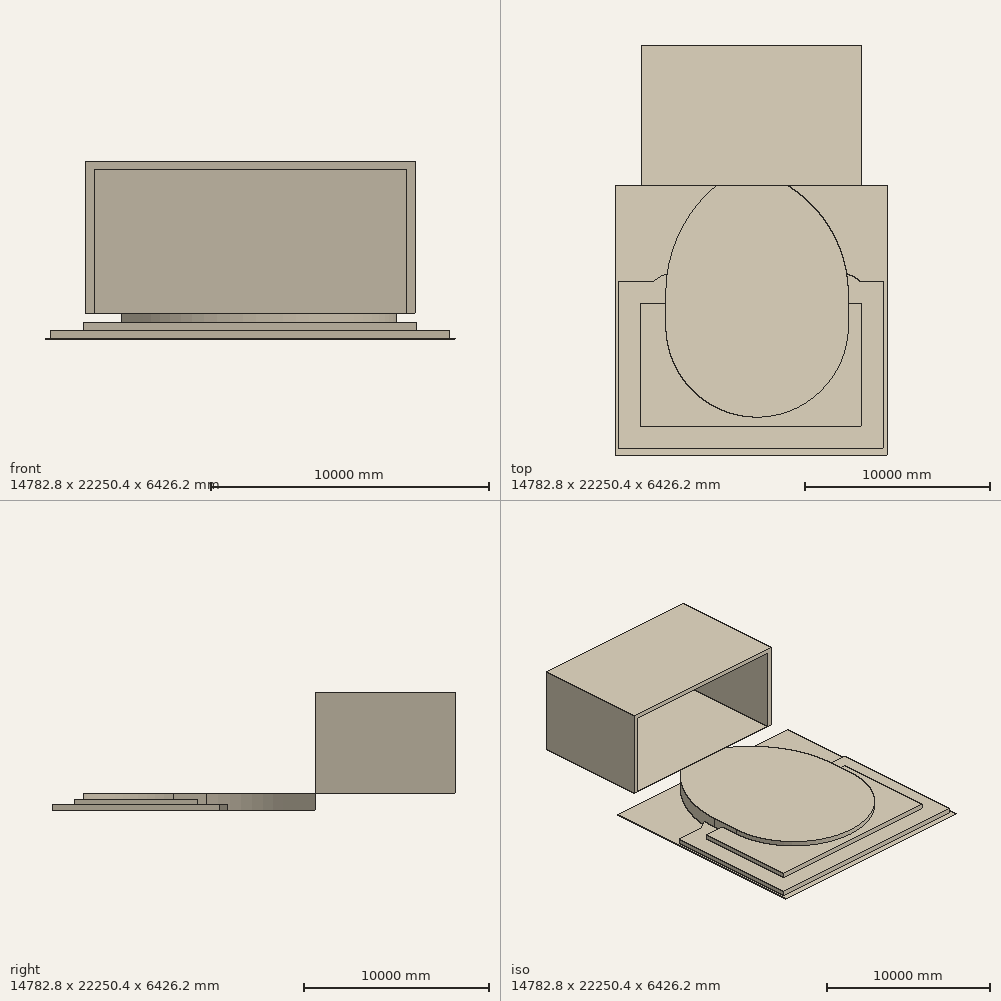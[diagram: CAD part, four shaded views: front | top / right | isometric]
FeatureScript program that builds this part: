
annotation { "Feature Type Name" : "Feature", "Feature Type Description" : "" }
export const myFeature = defineFeature(function(context is Context, id is Id, definition is map)
    precondition{}
    {
        {
            var Q0;
            Q0=qCreatedBy(makeId("Top.planeOp"),FACE);
            var sketch = newSketch(context, id + "F0", { "sketchPlane" : qUnion([Q0])});
            skLineSegment(sketch, "E0.bottom", {"start": v(-5413.18, 0) * mm, "end": v(9369.62, 0) * mm});
            skLineSegment(sketch, "E0.top", {"start": v(-5413.18, -14630.4) * mm, "end": v(9369.62, -14630.4) * mm});
            skLineSegment(sketch, "E0.left", {"start": v(-5413.18, 0) * mm, "end": v(-5413.18, -14630.4) * mm});
            skLineSegment(sketch, "E0.right", {"start": v(9369.62, 0) * mm, "end": v(9369.62, -14630.4) * mm});
            skSolve(sketch);
        }
        {
            var Q0;
            Q0=makeQuery(id+"F0.imprint","IMPRINT",FACE,{"disambiguationData":[TD([[makeQuery(id+"F0.imprint","IMPRINT",EDGE,{"derivedFrom":sQuery(id+"F0.wireOp",EDGE,"E0.bottom")}),-1.0]])]});
            extrude(context, id + "F1", {"entities" : qUnion([Q0]), "oppositeDirection" : true, "depth" : 25.4 * mm});
        }
        {
            var Q0;
            Q0=makeQuery(id+"F1.opExtrude","CAP_FACE",FACE,{"disambiguationData":[OSD([sQuery(id+"F0.wireOp",EDGE,"E0.bottom"),sQuery(id+"F0.wireOp",EDGE,"E0.top"),sQuery(id+"F0.wireOp",EDGE,"E0.left"),sQuery(id+"F0.wireOp",EDGE,"E0.right")])],"isStart":true});
            var sketch = newSketch(context, id + "F2", { "sketchPlane" : qUnion([Q0])});
            skArc(sketch, "E1", {"start": v(73.22, 0) * mm, "mid": v(-1968.15, -2645.58) * mm, "end": v(-2669.49, -5912.75) * mm});
            skArc(sketch, "E2.MirrorCS", {"start": v(3984.82, 0) * mm, "mid": v(6363.8, -2518.13) * mm, "end": v(7235.98, -5870.7) * mm});
            skLineSegment(sketch, "E3", {"start": v(2028.45, -12547.65) * mm, "end": v(2526.63, -12484.75) * mm});
            skArc(sketch, "E4", {"start": v(-2673.59, -7535.85) * mm, "mid": v(2315.04, -12554.16) * mm, "end": v(7241.23, -7474.54) * mm});
            skLineSegment(sketch, "E5", {"start": v(-2673.59, -7535.85) * mm, "end": v(-2668.95, -5701.93) * mm});
            skLineSegment(sketch, "E6", {"start": v(7241.92, -7684.86) * mm, "end": v(7235.98, -5870.7) * mm});
            skSolve(sketch);
        }
        {
            var Q0;
            {var subQ1=sQuery(id+"F2.wireOp",EDGE,"E2.MirrorCS");Q0=makeQuery(id+"F2.imprint","IMPRINT",FACE,{"disambiguationData":[TD([[makeQuery(id+"F2.imprint","IMPRINT",EDGE,{"derivedFrom":subQ1}),1.0]])]});}
            extrude(context, id + "F3", {"entities" : qUnion([Q0]), "operationType" : NewBodyOperationType.ADD, "depth" : 914.4 * mm});
        }
        {
            var Q0;
            Q0=makeQuery(id+"F0.imprint","IMPRINT",FACE,{"disambiguationData":[TD([[makeQuery(id+"F0.imprint","IMPRINT",EDGE,{"derivedFrom":sQuery(id+"F0.wireOp",EDGE,"E0.bottom")}),-1.0]])]});
            var sketch = newSketch(context, id + "F4", { "sketchPlane" : qUnion([Q0])});
            skLineSegment(sketch, "E7.2", {"start": v(-1479.8, -7544.99) * mm, "end": v(-1476.86, -6378.62) * mm});
            skArc(sketch, "E7.3", {"start": v(6047.48, -7491.98) * mm, "mid": v(2310.9, -11360.37) * mm, "end": v(-1479.8, -7544.99) * mm});
            skLineSegment(sketch, "E7.8", {"start": v(6043.84, -6378.63) * mm, "end": v(6047.48, -7491.98) * mm});
            skArc(sketch, "E8", {"start": v(-1476.86, -6378.62) * mm, "mid": v(-2073.76, -5892.8) * mm, "end": v(-2670.66, -6378.62) * mm});
            skArc(sketch, "E9", {"start": v(7237.65, -6378.63) * mm, "mid": v(6640.74, -5892.8) * mm, "end": v(6043.84, -6378.63) * mm});
            skLineSegment(sketch, "E10", {"start": v(-2670.66, -6378.62) * mm, "end": v(-4050.4, -6378.62) * mm});
            skLineSegment(sketch, "E11", {"start": v(-4050.4, -6378.62) * mm, "end": v(-4050.4, -13055.66) * mm});
            skLineSegment(sketch, "E12", {"start": v(-4050.4, -13055.66) * mm, "end": v(7961.94, -13055.66) * mm});
            skLineSegment(sketch, "E13", {"start": v(7961.94, -13055.66) * mm, "end": v(7961.94, -6378.62) * mm});
            skLineSegment(sketch, "E14", {"start": v(7961.94, -6378.62) * mm, "end": v(7237.65, -6378.63) * mm});
            skSolve(sketch);
        }
        {
            var Q0;
            Q0 = qSketchRegion(id + "F4", true);
            var Q1;
            Q1=sQuery(id+"F4.wireOp",EDGE,"E11");
            var Q2;
            Q2=sQuery(id+"F4.wireOp",EDGE,"E14");
            var Q3;
            Q3=sQuery(id+"F4.wireOp",EDGE,"E7.3");
            var Q4;
            Q4=sQuery(id+"F4.wireOp",EDGE,"E7.2");
            var Q5;
            Q5=sQuery(id+"F4.wireOp",EDGE,"E10");
            var Q6;
            Q6=sQuery(id+"F4.wireOp",EDGE,"E13");
            var Q7;
            Q7=sQuery(id+"F4.wireOp",EDGE,"E8");
            var Q8;
            Q8=sQuery(id+"F4.wireOp",EDGE,"E12");
            var Q9;
            Q9=sQuery(id+"F4.wireOp",EDGE,"E7.8");
            var Q10;
            Q10=sQuery(id+"F4.wireOp",EDGE,"E9");
            extrude(context, id + "F5", {"entities" : qUnion([Q0]), "surfaceEntities" : qUnion([Q1, Q2, Q3, Q4, Q5, Q6, Q7, Q8, Q9, Q10]), "depth" : 609.6 * mm});
        }
        {
            var Q0;
            Q0=makeQuery(id+"F0.imprint","IMPRINT",FACE,{"disambiguationData":[TD([[makeQuery(id+"F0.imprint","IMPRINT",EDGE,{"derivedFrom":sQuery(id+"F0.wireOp",EDGE,"E0.bottom")}),-1.0]])]});
            var sketch = newSketch(context, id + "F6", { "sketchPlane" : qUnion([Q0])});
            skLineSegment(sketch, "E15.0", {"start": v(-5244.2, -14249.46) * mm, "end": v(9155.74, -14249.46) * mm});
            skLineSegment(sketch, "E15.1", {"start": v(-5244.2, -5184.82) * mm, "end": v(-5244.2, -14249.46) * mm});
            skLineSegment(sketch, "E15.2", {"start": v(9155.74, -14249.46) * mm, "end": v(9155.74, -5184.81) * mm});
            skLineSegment(sketch, "E15.3", {"start": v(-3305.12, -5184.82) * mm, "end": v(-5244.2, -5184.82) * mm});
            skArc(sketch, "E15.4", {"start": v(-282.83, -6290.67) * mm, "mid": v(-1454.08, -4808.8) * mm, "end": v(-3305.12, -5184.82) * mm});
            skLineSegment(sketch, "E15.5", {"start": v(-286.03, -7555.2) * mm, "end": v(-282.83, -6290.67) * mm});
            skLineSegment(sketch, "E15.6", {"start": v(9155.74, -5184.81) * mm, "end": v(7872.1, -5184.83) * mm});
            skArc(sketch, "E15.7", {"start": v(7872.1, -5184.83) * mm, "mid": v(6020.8, -4808.9) * mm, "end": v(4849.75, -6291.24) * mm});
            skLineSegment(sketch, "E15.8", {"start": v(4849.75, -6291.24) * mm, "end": v(4853.74, -7511.8) * mm});
            skArc(sketch, "E15.9", {"start": v(4853.74, -7511.8) * mm, "mid": v(2306.09, -10166.57) * mm, "end": v(-286.03, -7555.2) * mm});
            skSolve(sketch);
        }
        {
            var Q0;
            Q0 = qSketchRegion(id + "F6", true);
            extrude(context, id + "F7", {"entities" : qUnion([Q0]), "depth" : 304.8 * mm});
        }
        {
            var Q0;
            Q0=makeQuery(id+"F0.imprint","IMPRINT",FACE,{"disambiguationData":[TD([[makeQuery(id+"F0.imprint","IMPRINT",EDGE,{"derivedFrom":sQuery(id+"F0.wireOp",EDGE,"E0.bottom")}),-1.0]])]});
            var sketch = newSketch(context, id + "F8", { "sketchPlane" : qUnion([Q0])});
            skLineSegment(sketch, "E16", {"start": v(-1121.86, -1312.55) * mm, "end": v(5456.74, -1312.55) * mm});
            skFitSpline(sketch, "E17", {"points": [v(-1121.86, -1312.55) * mm, v(-807.54, -910.36) * mm, v(-441.81, -535.41) * mm, v(80.46, -31.36) * mm, v(132.47, -18.66) * mm], "startDerivative": vector(1110.36, 1498.46) * mm, "endDerivative": vector(440.99, -31.9) * mm});
            skFitSpline(sketch, "E18", {"points": [v(5456.74, -1312.55) * mm, v(5190.5, -984.3) * mm, v(4777, -643.83) * mm, v(4221.13, -224.5) * mm, v(4001.1, -18.66) * mm, v(4024.04, -41.23) * mm], "startDerivative": vector(-1170.4, 1588.76) * mm, "endDerivative": vector(204.9, -1378.26) * mm});
            skLineSegment(sketch, "E19", {"start": v(132.47, -18.66) * mm, "end": v(4001.1, -18.66) * mm});
            skSolve(sketch);
        }
        {
            var Q0;
            Q0 = qSketchRegion(id + "F8", true);
            extrude(context, id + "F9", {"entities" : qUnion([Q0]), "operationType" : NewBodyOperationType.ADD, "depth" : 914.4 * mm});
        }
        {
            var Q0;
            Q0=makeQuery(id+"F0.imprint","IMPRINT",FACE,{"disambiguationData":[TD([[makeQuery(id+"F0.imprint","IMPRINT",EDGE,{"derivedFrom":sQuery(id+"F0.wireOp",EDGE,"E0.bottom")}),-1.0]])]});
            var sketch = newSketch(context, id + "F10", { "sketchPlane" : qUnion([Q0])});
            skLineSegment(sketch, "E20.bottom", {"start": v(376.74, -1334.32) * mm, "end": v(4034.34, -1334.32) * mm});
            skLineSegment(sketch, "E20.top", {"start": v(376.74, -6211.12) * mm, "end": v(4034.34, -6211.12) * mm});
            skLineSegment(sketch, "E20.left", {"start": v(376.74, -1334.32) * mm, "end": v(376.74, -6211.12) * mm});
            skLineSegment(sketch, "E20.right", {"start": v(4034.34, -1334.32) * mm, "end": v(4034.34, -6211.12) * mm});
            skSolve(sketch);
        }
        {
            var Q0;
            Q0 = qSketchRegion(id + "F10", true);
            extrude(context, id + "F11", {"entities" : qUnion([Q0]), "operationType" : NewBodyOperationType.ADD, "depth" : 914.4 * mm});
        }
        {
            var Q0;
            Q0=makeQuery(id+"F3.opExtrude","CAP_FACE",FACE,{"disambiguationData":[OSD([sQuery(id+"F0.wireOp",EDGE,"E0.bottom"),sQuery(id+"F0.wireOp",EDGE,"E0.top"),sQuery(id+"F0.wireOp",EDGE,"E0.left"),sQuery(id+"F0.wireOp",EDGE,"E0.right"),sQuery(id+"F2.wireOp",EDGE,"E1"),sQuery(id+"F2.wireOp",EDGE,"E2.MirrorCS"),sQuery(id+"F2.wireOp",EDGE,"E4"),sQuery(id+"F2.wireOp",EDGE,"E5"),sQuery(id+"F2.wireOp",EDGE,"E6")])],"isStart":false});
            var sketch = newSketch(context, id + "F12", { "sketchPlane" : qUnion([Q0])});
            skLineSegment(sketch, "E21.bottom", {"start": v(-3965.38, 0) * mm, "end": v(7921.82, 0) * mm});
            skLineSegment(sketch, "E21.top", {"start": v(-3965.38, 7620) * mm, "end": v(7921.82, 7620) * mm});
            skLineSegment(sketch, "E21.left", {"start": v(-3965.38, 0) * mm, "end": v(-3965.38, 7620) * mm});
            skLineSegment(sketch, "E21.right", {"start": v(7921.82, 0) * mm, "end": v(7921.82, 7620) * mm});
            skSolve(sketch);
        }
        {
            var Q0;
            Q0 = qSketchRegion(id + "F12", true);
            extrude(context, id + "F13", {"entities" : qUnion([Q0]), "operationType" : NewBodyOperationType.ADD, "depth" : 5486.4 * mm, "offsetDistance" : 25.4 * mm});
        }
        {
            var Q0;
            Q0=makeQuery(id+"F13.opExtrude","SWEPT_FACE",FACE,{"disambiguationData":[OSD([sQuery(id+"F12.wireOp",EDGE,"E21.bottom")])]});
            var sketch = newSketch(context, id + "F14", { "sketchPlane" : qUnion([Q0])});
            skLineSegment(sketch, "E22.bottom", {"start": v(-3660.58, 6096) * mm, "end": v(7617.02, 6096) * mm});
            skLineSegment(sketch, "E22.top", {"start": v(7617.02, 927.1) * mm, "end": v(-3660.58, 927.1) * mm});
            skLineSegment(sketch, "E22.left", {"start": v(-3660.58, 6096) * mm, "end": v(-3660.58, 927.1) * mm});
            skLineSegment(sketch, "E22.right", {"start": v(7617.02, 6096) * mm, "end": v(7617.02, 927.1) * mm});
            skSolve(sketch);
        }
        {
            var Q0;
            Q0 = qSketchRegion(id + "F14", true);
            extrude(context, id + "F15", {"entities" : qUnion([Q0]), "operationType" : NewBodyOperationType.REMOVE, "oppositeDirection" : true, "depth" : 7010.4 * mm});
        }
    });
